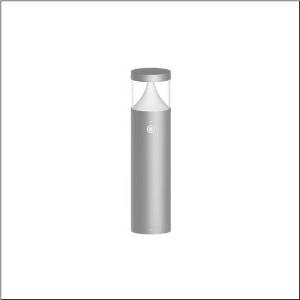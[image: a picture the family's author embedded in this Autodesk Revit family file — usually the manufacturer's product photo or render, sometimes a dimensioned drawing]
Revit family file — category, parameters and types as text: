
# Revit family: cl_31_poller_60_sensor_5cl434803
name_source: partatom
category: Lighting Fixtures
units: mm (PartAtom-declared; Revit-internal decimal feet)

## family parameters
Cut with Voids When Loaded = No
Host = Face
Light Source = No
Part Type = Normal
Room Calculation Point = No
Round Connector Dimension = Use Diameter
Shared = No

## types (1)
- --- (1 x LED, 1500 lm, 14 W, 3000K)
    Apparent Load = 14 VA
    CIE Flux Codes = 19 66 88 92 100
    Color Rendering = 80
    Color Temperature = 3000K
    Default Elevation = 1800 mm
    Description = CL 31 Bollard 60 Sensor, bollard luminaire, primary light control with lens, of PC, primary optical cover: cover panel, of PC, transparent, secondary light control with reflector, of PC, primary light characteristic: asymmetric, LED, rated luminous flux: 1.500lm, luminous efficacy: 107lm/W, light colour: 830, colour temperature: 3000K, control gear: DALI, with terminal, 5-pole, max. 2.5mm², mains connection: 220..240V, AC, 50/60Hz, rated input power: 14W, luminaire housing, of aluminium, powder-coated, Siteco® metallic grey, diameter: 170mm, height: 600mm, PIR sensor, protection rating (complete): IP65, insulation class (complete): insulation class I (protective earthing), certification: CE, ENEC, impact resistance: IK08, permissible operating ambient temperature for outdoor applications: -20..+50°C, packaging unit: 1 piece
    Height = 200 mm  [stored 0.656168 ft]
    Lamp = 1 x LED
    Lamp Light Flux = 1500 lm
    Lamp Power = 14 W
    Lamp count = 1
    Length = 170 mm  [stored 0.557743 ft]
    Luminous efficacy = 107 lm/W
    Manufacturer = Siteco
    ModVariant = No
    Model = 5CL434803
    Mounting Place = Floor
    Mounting Type = Freestanding
    Number of Poles = 1
    OnlyDefault = Yes
    Power Factor = 1
    Product Name = CL 31 Poller 60 Sensor
    Product group = bollard luminaire
    ProductGroupID = 1304
    Protection Class = Protection class I
    Protection Degree = IP 65
    RLX_Detail_Level = 1
    RLX_Emergency_Light_Flux = 0 lm
    RLX_Emergency_Type = 0
    RLX_Emergency_Type_DB = No
    RlxData = <blob elided: 64609 chars, md5=6e8bc000>
    Socket = socket
    Standby Power = 0 W
    System Light Flux = 1500 lm
    System Power = 14 W
    Type Comments = factory setting: luminous flux: 100 % | dim-lin: 254 | 350 mA
    Type Image = l_1006901.jpg
    URL = http://relux.com
    VarID = @adj_216463
    Voltage = 0 V
    Weight = 0.00 kg
    Width = 0 mm  [stored 0 ft]

note: [stored X ft] marks values corroborated as IEEE doubles in the binary element streams (Revit-internal decimal feet)

## geometry (parser evidence)
native form markers: Blend x4, Sweep x12
no freeform markers — native parametric forms only
